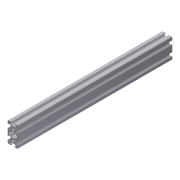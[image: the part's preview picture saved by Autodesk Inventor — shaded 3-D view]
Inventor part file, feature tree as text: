
AUTODESK INVENTOR PART (.ipt)
format: ipt  version: 2013 (Build 170138000, 138)  size: 463,360 bytes
history: native  units: in
note: dims shown in document units (in); Inventor stores cm internally (conversion verified against a paired STEP export)
features: other x3, extrude x1, sketch x1
ambient origin geometry x8: Origin, YZ Plane, XZ Plane, XY Plane, X Axis, Y Axis, Z Axis, Center Point
bodies: Solid1 (feature_tree)
feature tree (5):
  other  "Blocks"
  extrude  "Extrusion1"  [1 undecoded]
  sketch  "Sketch1"  dims[d1=0.0in]
  other  "Bosch 20x40 profile"
  other  "Bosch 20x40 profile:1"
note: 1 required parameter value undecoded (feature->parameter linkage not recoverable at this tier; creation-order binding heuristic only, values carry confidence <= 0.55)
